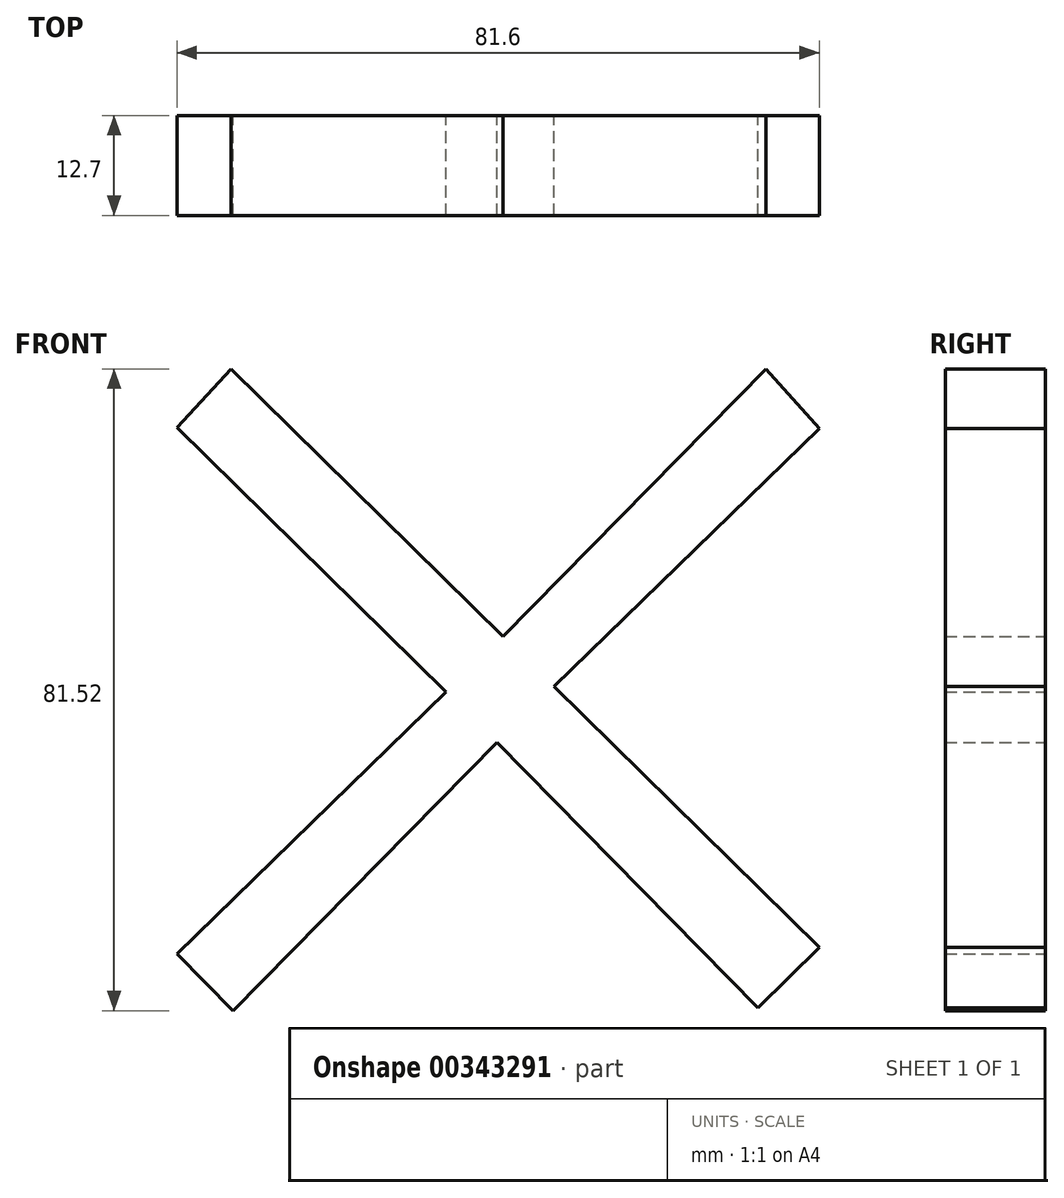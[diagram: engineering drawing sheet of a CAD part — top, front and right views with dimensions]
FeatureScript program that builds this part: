
annotation { "Feature Type Name" : "Feature", "Feature Type Description" : "" }
export const myFeature = defineFeature(function(context is Context, id is Id, definition is map)
    precondition{}
    {
        {
            var Q0;
            Q0=qCreatedBy(makeId("Front.planeOp"),FACE);
            var sketch = newSketch(context, id + "F0", { "sketchPlane" : qUnion([Q0])});
            skLineSegment(sketch, "E0", {"start": v(-40.6, 33.7) * mm, "end": v(-33.71, 41.16) * mm});
            skLineSegment(sketch, "E1", {"start": v(-40.6, 33.7) * mm, "end": v(-2.48, -3.79) * mm});
            skLineSegment(sketch, "E2", {"start": v(34.25, 41.16) * mm, "end": v(41, 33.56) * mm});
            skLineSegment(sketch, "E3", {"start": v(34.25, 41.16) * mm, "end": v(0.84, 7.18) * mm});
            skLineSegment(sketch, "E4", {"start": v(41, 33.56) * mm, "end": v(0.04, -6.27) * mm});
            skLineSegment(sketch, "E5", {"start": v(-2.48, -3.79) * mm, "end": v(0.04, -6.27) * mm});
            skLineSegment(sketch, "E6", {"start": v(-33.71, 41.16) * mm, "end": v(0.84, 7.18) * mm});
            skLineSegment(sketch, "E7", {"start": v(0.84, 7.18) * mm, "end": v(-40.6, -33.12) * mm});
            skLineSegment(sketch, "E8", {"start": v(0.84, 7.18) * mm, "end": v(41, -32.3) * mm});
            skLineSegment(sketch, "E9", {"start": v(41, -32.3) * mm, "end": v(33.19, -39.98) * mm});
            skLineSegment(sketch, "E10", {"start": v(0.04, -6.27) * mm, "end": v(-33.48, -40.36) * mm});
            skLineSegment(sketch, "E11", {"start": v(-40.6, -33.12) * mm, "end": v(-33.48, -40.36) * mm});
            skLineSegment(sketch, "E12", {"start": v(0.04, -6.27) * mm, "end": v(33.19, -39.98) * mm});
            skSolve(sketch);
        }
        {
            var Q0;
            Q0 = qSketchRegion(id + "F0", true);
            extrude(context, id + "F1", {"entities" : qUnion([Q0]), "depth" : 12.7 * mm});
        }
    });
